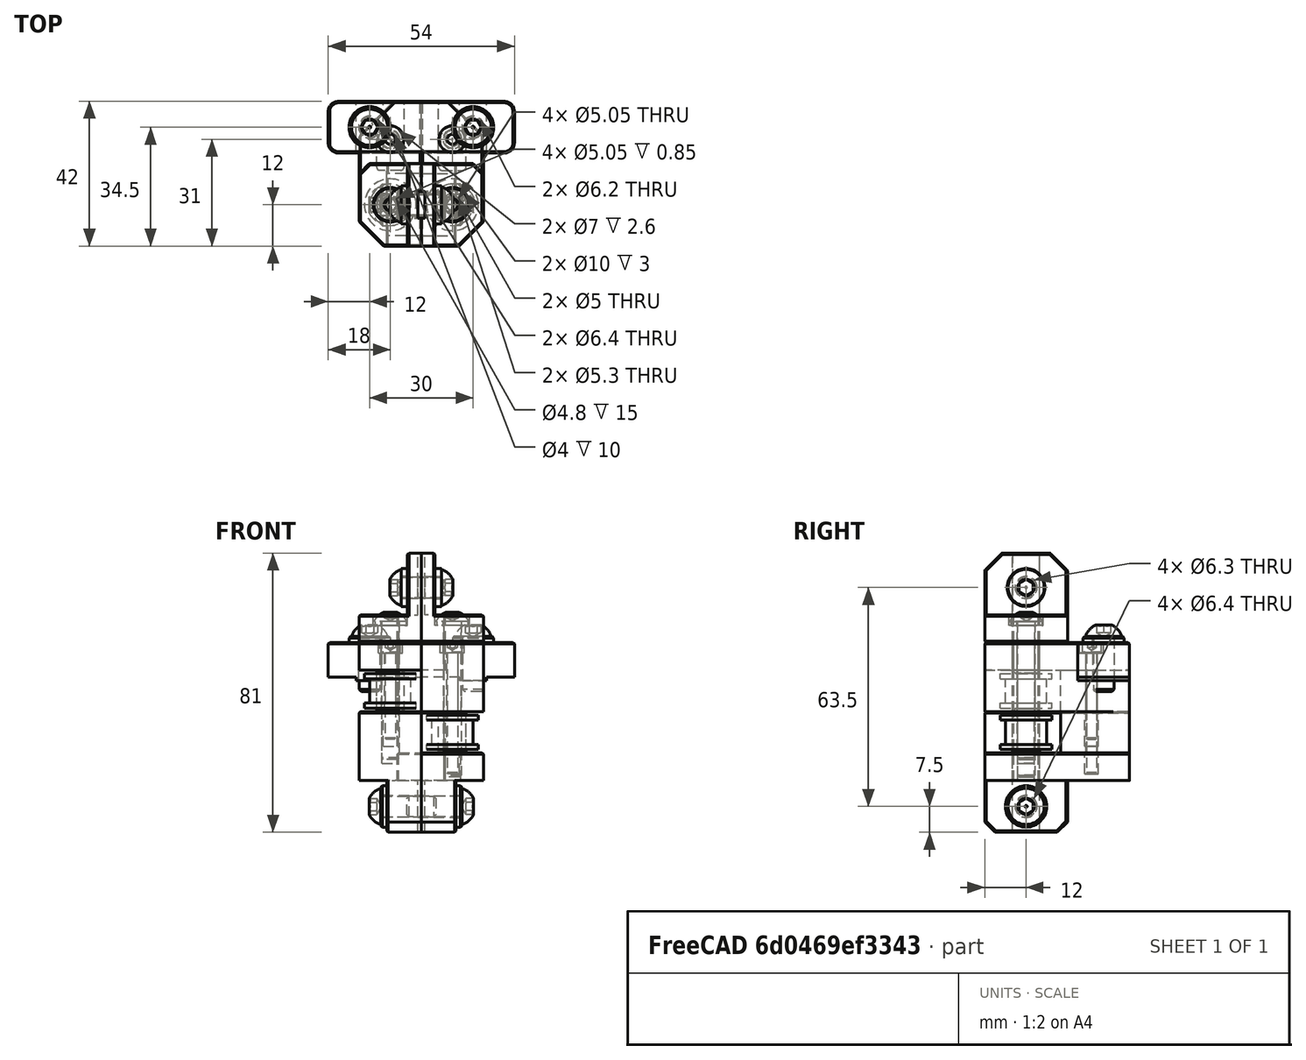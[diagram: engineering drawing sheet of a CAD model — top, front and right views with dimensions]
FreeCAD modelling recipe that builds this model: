
FCSTD DOCUMENT  (FreeCAD 0.19R24291 (Git))
Label: front-idler-assembly
License: Other
LicenseURL: GPL3
objects: Part::FeaturePython×19, Part::Feature×12, App::Part×2
note: 31 computed .brp shape members not serialized (recipe doc carries the construction recipe); baked Part::Feature solids carry a one-line shape summary decoded from their .brp

FEATURE [Part::Feature] Cut002002002002001  label="idler-washer004"
  Placement = pos=(-2,0,0) rot=(0,0,1;0rad)
  shape: bbox 8 x 8 x 0.85 mm, 4 faces (baked)
FEATURE [Part::Feature] Cut002002002001001  label="idler-washer003"
  Placement = pos=(-2,0,0) rot=(0,0,1;0rad)
  shape: bbox 8 x 8 x 0.85 mm, 4 faces (baked)
FEATURE [Part::Feature] Cut002002002003  label="smooth-idler-6mm002"
  Placement = pos=(-2,0,0) rot=(0,0,1;0rad)
  shape: bbox 15 x 15 x 10 mm, 8 faces (baked)
FEATURE [Part::Feature] Part__Mirroring004002  label="smooth-idler-6mm"
  Placement = pos=(2,0,0) rot=(0,0,1;0rad)
  shape: bbox 15 x 15 x 10 mm, 8 faces (baked)
FEATURE [Part::Feature] Part__Mirroring003001  label="idler-washer001"
  Placement = pos=(2,0,0) rot=(0,0,1;0rad)
  shape: bbox 8 x 8 x 0.85 mm, 4 faces (baked)
FEATURE [Part::Feature] Part__Mirroring004001  label="idler-washer002"
  Placement = pos=(2,0,0) rot=(0,0,1;0rad)
  shape: bbox 8 x 8 x 0.85 mm, 4 faces (baked)
FEATURE [Part::Feature] Part__Mirroring004003  label="Chamfer013 (Mirror #2)001"
  shape: bbox 25 x 42 x 35 mm, 51 faces (baked)
FEATURE [Part::Feature] Chamfer019001  label="Chamfer020"
  shape: bbox 25 x 42 x 23 mm, 51 faces (baked)
FEATURE [Part::Feature] Chamfer020001  label="top-exp001"
  shape: bbox 45 x 42 x 32 mm, 61 faces (baked)
FEATURE [Part::Feature] Part__Mirroring001  label="top-exp (Mirror #1)001"
  shape: bbox 45 x 42 x 20 mm, 62 faces (baked)
FEATURE [Part::FeaturePython] Screw  label="M3x25-Screw"  # Fasteners workbench fastener (typed FeaturePython)
  Placement = pos=(-9,34,37) rot=(0,0,1;0rad)
  baseObject = -> Part__Mirroring001 [Edge155]
  diameter = 4
  invert = true
  length = 10
  lengthCustom = 25
  matchOuter = true
  offset = 0
  thread = false
  type = 33
FEATURE [Part::FeaturePython] Washer  label="M6-Washer"  # Fasteners workbench fastener (typed FeaturePython)
  Placement = pos=(15,37.5,40) rot=(0,0,1;0rad)
  baseObject = -> Part__Mirroring001 [Edge44]
  diameter = 2
  invert = true
  matchOuter = true
  offset = 0
  type = 4
FEATURE [Part::FeaturePython] Screw001  label="M6x16-Screw"  # Fasteners workbench fastener (typed FeaturePython)
  Placement = pos=(15,37.5,41.8) rot=(0,0,1;0rad)
  baseObject = -> Washer [Edge1]
  diameter = 4
  invert = false
  length = 3
  lengthCustom = 16
  matchOuter = true
  offset = 0
  thread = false
  type = 39
FEATURE [Part::FeaturePython] Washer001  label="M6-Washer001"  # Fasteners workbench fastener (typed FeaturePython)
  Placement = pos=(-10,15,-7.5) rot=(0,-1,0;1.5708rad)
  baseObject = -> Part__Mirroring004003 [Edge84]
  diameter = 2
  invert = true
  matchOuter = true
  offset = 0
  type = 4
FEATURE [Part::FeaturePython] Screw003  label="M6x16-Screw001"  # Fasteners workbench fastener (typed FeaturePython)
  Placement = pos=(-11.8,15,-7.5) rot=(0,-1,0;1.5708rad)
  baseObject = -> Washer001 [Edge1]
  diameter = 4
  invert = false
  length = 3
  lengthCustom = 16
  matchOuter = true
  offset = 0
  thread = false
  type = 39
FEATURE [Part::FeaturePython] Washer002  label="M6-Washer002"  # Fasteners workbench fastener (typed FeaturePython)
  Placement = pos=(-15,37.5,40) rot=(0,0,1;0rad)
  baseObject = -> Chamfer020001 [Edge56]
  diameter = 2
  invert = false
  matchOuter = true
  offset = 0
  type = 4
FEATURE [Part::FeaturePython] Screw006  label="M3x35-Screw"  # Fasteners workbench fastener (typed FeaturePython)
  Placement = pos=(9,34,37) rot=(0,0,1;0rad)
  baseObject = -> Chamfer020001 [Edge152]
  diameter = 4
  invert = false
  length = 10
  lengthCustom = 35
  matchOuter = true
  offset = 0
  thread = false
  type = 33
FEATURE [Part::FeaturePython] Washer003  label="M6-Washer003"  # Fasteners workbench fastener (typed FeaturePython)
  Placement = pos=(10,15,-7.5) rot=(0,1,0;1.5708rad)
  baseObject = -> Chamfer019001 [Edge86]
  diameter = 2
  invert = false
  matchOuter = true
  offset = 0
  type = 4
FEATURE [Part::FeaturePython] Screw007  label="M6x16-Screw003"  # Fasteners workbench fastener (typed FeaturePython)
  Placement = pos=(11.8,15,-7.5) rot=(0,1,0;1.5708rad)
  baseObject = -> Washer003 [Edge1]
  diameter = 4
  invert = false
  length = 13
  lengthCustom = 16
  matchOuter = true
  offset = 0
  thread = false
  type = 39
FEATURE [Part::Feature] Cut002002002007004004001001  label="top-support002"
  shape: bbox 25 x 24 x 26 mm, 66 faces (baked)
FEATURE [Part::Feature] Part__Mirroring004004  label="top-support002 (Mirror #1)001"
  shape: bbox 25 x 24 x 26 mm, 66 faces (baked)
FEATURE [Part::FeaturePython] Washer004  label="M5-Washer"  # Fasteners workbench fastener (typed FeaturePython)
  Placement = pos=(-9,15,45) rot=(0,0,1;0rad)
  baseObject = -> Part__Mirroring004004 [Edge154]
  diameter = 6
  invert = true
  matchOuter = true
  offset = 0
  type = 5
FEATURE [Part::FeaturePython] Washer005  label="M6-Washer004"  # Fasteners workbench fastener (typed FeaturePython)
  Placement = pos=(-4,15,56) rot=(0,-1,0;1.5708rad)
  baseObject = -> Part__Mirroring004004 [Edge25]
  diameter = 7
  invert = false
  matchOuter = true
  offset = 0
  type = 5
FEATURE [Part::FeaturePython] Screw009  label="M6x12-Screw"  # Fasteners workbench fastener (typed FeaturePython)
  Placement = pos=(-5.8,15,56) rot=(0,-1,0;1.5708rad)
  baseObject = -> Washer005 [Edge1]
  diameter = 4
  invert = false
  length = 1
  lengthCustom = 12
  matchOuter = true
  offset = 0
  thread = false
  type = 39
FEATURE [Part::FeaturePython] Washer006  label="M5-Washer001"  # Fasteners workbench fastener (typed FeaturePython)
  Placement = pos=(-9,15,45) rot=(0,0,1;0rad)
  baseObject = -> Part__Mirroring004004 [Edge154]
  diameter = 6
  invert = true
  matchOuter = true
  offset = 0
  type = 5
FEATURE [Part::FeaturePython] Screw010  label="M5x40-Screw"  # Fasteners workbench fastener (typed FeaturePython)
  Placement = pos=(-9,15,46.1) rot=(0,0,1;0rad)
  baseObject = -> Washer006 [Edge1]
  diameter = 3
  invert = false
  length = 9
  lengthCustom = 40
  matchOuter = true
  offset = 0
  thread = false
  type = 39
FEATURE [App::Part] Part001  label="right-idler"
  Group = -> [Part__Mirroring004002,Part__Mirroring003001,Part__Mirroring004001,Part__Mirroring004003,Part__Mirroring001,Washer,Screw001,Screw,Screw003,Washer001,Part__Mirroring004004,Screw010,Washer004,Washer006,Screw009,Washer005]
  Origin = -> Origin001
FEATURE [Part::FeaturePython] Screw011  label="M6x16-Screw004"  # Fasteners workbench fastener (typed FeaturePython)
  Placement = pos=(-15,37.5,41.8) rot=(0,0,1;0rad)
  baseObject = -> Washer002 [Edge1]
  diameter = 4
  invert = false
  length = 3
  lengthCustom = 16
  matchOuter = true
  offset = 0
  thread = false
  type = 39
FEATURE [Part::FeaturePython] Washer007  label="M5-Washer002"  # Fasteners workbench fastener (typed FeaturePython)
  Placement = pos=(9,15,45) rot=(0,0,1;0rad)
  baseObject = -> Cut002002002007004004001001 [Edge154]
  diameter = 6
  invert = false
  matchOuter = true
  offset = 0
  type = 5
FEATURE [Part::FeaturePython] Washer008  label="M6-Washer005"  # Fasteners workbench fastener (typed FeaturePython)
  Placement = pos=(4,15,56) rot=(0,1,0;1.5708rad)
  baseObject = -> Cut002002002007004004001001 [Edge25]
  diameter = 7
  invert = true
  matchOuter = true
  offset = 0
  type = 5
FEATURE [Part::FeaturePython] Screw012  label="M6x12-Screw001"  # Fasteners workbench fastener (typed FeaturePython)
  Placement = pos=(5.8,15,56) rot=(0,1,0;1.5708rad)
  baseObject = -> Washer008 [Edge1]
  diameter = 4
  invert = false
  length = 1
  lengthCustom = 12
  matchOuter = true
  offset = 0
  thread = false
  type = 39
FEATURE [Part::FeaturePython] Screw013  label="M5x45-Screw"  # Fasteners workbench fastener (typed FeaturePython)
  Placement = pos=(9,15,46.1) rot=(0,0,1;0rad)
  baseObject = -> Washer007 [Edge1]
  diameter = 3
  invert = false
  length = 10
  lengthCustom = 45
  matchOuter = true
  offset = 0
  thread = false
  type = 39
FEATURE [App::Part] Part  label="left-idler"
  Group = -> [Cut002002002002001,Cut002002002001001,Cut002002002003,Chamfer019001,Chamfer020001,Screw006,Washer002,Screw007,Washer003,Cut002002002007004004001001,Screw011,Washer008,Screw013,Screw012,Washer007]
  Origin = -> Origin
